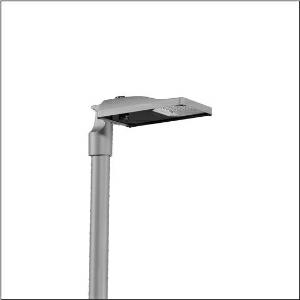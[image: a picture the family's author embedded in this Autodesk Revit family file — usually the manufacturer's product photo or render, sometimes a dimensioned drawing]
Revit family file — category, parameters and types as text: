
# Revit family: streetlight_sl_31_micro___st0_5a_5xh5b31t08da_db8b
name_source: partatom
category: Lighting Fixtures
units: mm (PartAtom-declared; Revit-internal decimal feet)

## family parameters
Cut with Voids When Loaded = No
Host = Face
Light Source = No
Part Type = Normal
Room Calculation Point = No
Round Connector Dimension = Use Diameter
Shared = No

## types (1)
- --- (1 x LED, 4940 lm, 37.7 W, 3000K)
    Apparent Load = 38 VA
    CIE Flux Codes = 41 75 97 100 100
    Color Rendering = 70
    Color Temperature = 3000K
    Default Elevation = 1800 mm
    Description = Streetlight SL 31 micro D4i, Desk-Remote mast luminaire for post-top, side-entry; light control with lens of PMMA; light distribution: ST0.5a, direct asymmetric distribution, for standard-compliant lighting for roads and squares; LED: luminous flux: 4.940lm, light colour: 730, colour temperature: 3000K; luminous efficacy: 131lm/W; control: pre-setting: logarithmic dimming characteristic, flexible luminous flux parameterisation, time-dependent luminous flux control, constant luminous flux control, power reduction, intelligent temperature release in ECG and LED module, overheat protection; luminaire housing, of diecast aluminium, Siteco® metallic grey (DB 702S), corrosivity category C5 high according to DIN EN ISO 12944; cover of toughened safety glass, transparent, opened without tools; mast flange of diecast aluminium, Siteco® metallic grey (DB 702S), spigot size: 76/60mm, mast flange included unmounted; with cable H07RN-F 2x 1.5mm², cable length: 6,5m, connection cable pre-assembled; mains connection: 220..240V, AC, 50/60Hz; power consumption (at start of service life): 37,7W / (at end of service life): 40,9W / (with reduced operation 50%): 16,3W; protection rating (complete): IP66; insulation class (complete): insulation class II (safety insulation); impact resistance: IK09; certification: CE, ENEC, ENEC+, VDE, UKCA, ZD4i; permissible operating ambient temperature for outdoor applications: -40..+50°C; packaging unit: 1 piece

Light Distribution: ST0.5a
    Height = 76 mm
    Lamp = 1 x LED
    Lamp Light Flux = 4940 lm
    Lamp Power = 37.7 W
    Lamp count = 1
    Length = 467 mm
    Luminous efficacy = 131 lm/W
    Manufacturer = Siteco
    ModVariant = No
    Model = 5XH5B31T08DA
    Number of Poles = 1
    OnlyDefault = Yes
    Power Factor = 1
    Product Name = Streetlight SL 31 micro | ST0.5a
    Product group = mast luminaire | pylon top
    ProductGroupID = 6100
    Protection Class = Protection class II
    Protection Degree = IP 66
    RLX_Detail_Level = 1
    RLX_Emergency_Light_Flux = 0 lm
    RLX_Emergency_Type = 0
    RLX_Emergency_Type_DB = No
    RlxData = <blob elided: 55209 chars, md5=d79fc37c>
    Socket = socket
    Standby Power = 0 W
    System Light Flux = 4940 lm
    System Power = 38 W
    Type Comments = factory setting: luminous flux: 100 % | dim-lin: 254 | 745 mA
    Type Image = l_1300315.jpg
    URL = http://relux.com
    VarID = @adj_069107
    Voltage = 0 V
    Weight = 0.00 kg
    Width = 265 mm

## geometry (parser evidence)
native form markers: Blend x4, Sweep x11
no freeform markers — native parametric forms only
